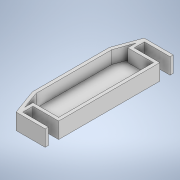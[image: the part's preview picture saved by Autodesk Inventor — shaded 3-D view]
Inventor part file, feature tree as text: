
AUTODESK INVENTOR PART (.ipt)
format: ipt  version: 2020 (Build 240168000, 168)  size: 162,304 bytes
history: native  units: in
note: dims shown in document units (in); Inventor stores cm internally (conversion verified against a paired STEP export)
features: extrude x2, sketch x2, projected_geometry x1
ambient origin geometry x8: Origin, YZ Plane, XZ Plane, XY Plane, X Axis, Y Axis, Z Axis, Center Point
bodies: Solid1 (feature_tree)
feature tree (5):
  extrude  "Extrusion1"  Depth=10.0in
  extrude  "Extrusion4"  Depth=2.0in
  sketch  "Sketch1"  dims[d0=3.0in d1=10.0in]
  sketch  "Sketch4"  dims[d2=0.481in d3=2.0in d4=0.25in d5=0.0in d6=2.0in d17=0.25in d18=0.8in d19=0.25in d20=1.0in d21=0.0in]
  projected_geometry  "Projected Loop3"
